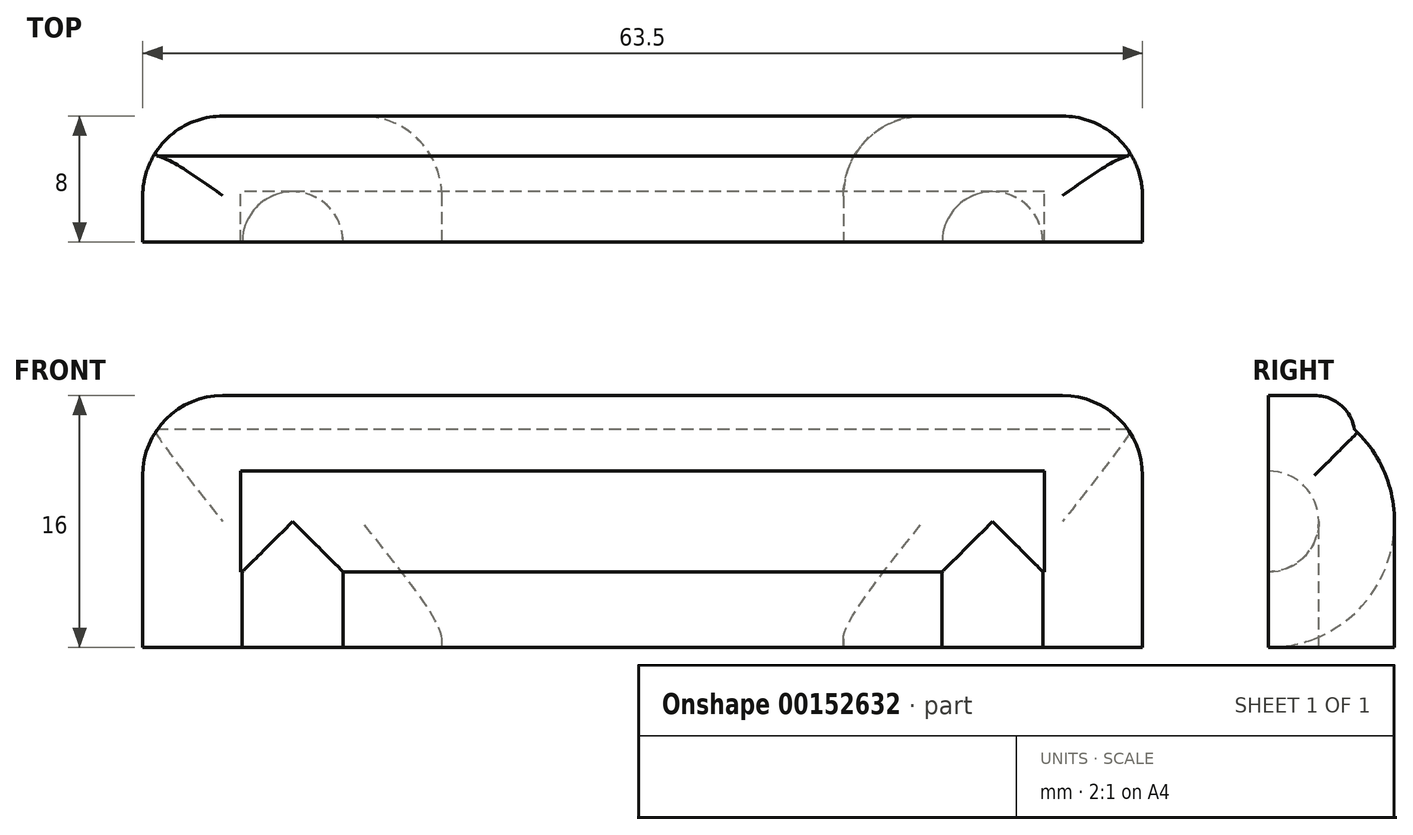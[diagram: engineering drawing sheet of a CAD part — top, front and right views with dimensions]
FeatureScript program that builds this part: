
annotation { "Feature Type Name" : "Feature", "Feature Type Description" : "" }
export const myFeature = defineFeature(function(context is Context, id is Id, definition is map)
    precondition{}
    {
        {
            var Q0;
            Q0=qCreatedBy(makeId("Right.planeOp"),FACE);
            var sketch = newSketch(context, id + "F0", { "sketchPlane" : qUnion([Q0])});
            skCircle(sketch, "E0", {"center": v(0, 0) * mm, "radius": 8 * mm});
            skSolve(sketch);
        }
        {
            var Q0;
            Q0 = qSketchRegion(id + "F0", true);
            extrude(context, id + "F1", {"entities" : qUnion([Q0]), "depth" : 63.5 * mm});
        }
        {
            var Q0;
            Q0=qCreatedBy(makeId("Top.planeOp"),FACE);
            var sketch = newSketch(context, id + "F2", { "sketchPlane" : qUnion([Q0])});
            skLineSegment(sketch, "E1.bottom", {"start": v(0, -8) * mm, "end": v(19, -8) * mm});
            skLineSegment(sketch, "E1.top", {"start": v(0, 8) * mm, "end": v(19, 8) * mm});
            skLineSegment(sketch, "E1.left", {"start": v(0, -8) * mm, "end": v(0, 8) * mm});
            skLineSegment(sketch, "E1.right", {"start": v(19, -8) * mm, "end": v(19, 8) * mm});
            skLineSegment(sketch, "E2.bottom", {"start": v(63.5, 8) * mm, "end": v(44.5, 8) * mm});
            skLineSegment(sketch, "E2.top", {"start": v(63.5, -8) * mm, "end": v(44.5, -8) * mm});
            skLineSegment(sketch, "E2.left", {"start": v(63.5, 8) * mm, "end": v(63.5, -8) * mm});
            skLineSegment(sketch, "E2.right", {"start": v(44.5, 8) * mm, "end": v(44.5, -8) * mm});
            skSolve(sketch);
        }
        {
            var Q0;
            Q0 = qSketchRegion(id + "F2", true);
            extrude(context, id + "F3", {"entities" : qUnion([Q0]), "operationType" : NewBodyOperationType.ADD, "oppositeDirection" : true, "depth" : 16 * mm / 2});
        }
        {
            var Q0;
            Q0=qCreatedBy(makeId("Top.planeOp"),FACE);
            var sketch = newSketch(context, id + "F4", { "sketchPlane" : qUnion([Q0])});
            skCircle(sketch, "E3", {"center": v(9.53, 0) * mm, "radius": 3.2 * mm});
            skCircle(sketch, "E4", {"center": v(53.98, 0) * mm, "radius": 3.2 * mm});
            skSolve(sketch);
        }
        {
            var Q0;
            Q0 = qSketchRegion(id + "F4", true);
            extrude(context, id + "F5", {"entities" : qUnion([Q0]), "operationType" : NewBodyOperationType.REMOVE, "oppositeDirection" : true, "depth" : 25.4 * mm});
        }
        {
            var Q0;
            Q0=qCreatedBy(makeId("Right.planeOp"),FACE);
            cPlane(context, id + "F6", {"entities" : qUnion([Q0]), "cplaneType" : CPlaneType.OFFSET, "offset" : 9.52 * mm, "width" : 152.4 * mm, "height" : 152.4 * mm});
        }
        {
            var Q0;
            Q0=qCreatedBy(id+"F6.planeOp",FACE);
            var sketch = newSketch(context, id + "F7", { "sketchPlane" : qUnion([Q0])});
            skCircle(sketch, "E5", {"center": v(0, 0) * mm, "radius": 3.2 * mm});
            skSolve(sketch);
        }
        {
            var Q0;
            Q0 = qSketchRegion(id + "F7", true);
            extrude(context, id + "F8", {"entities" : qUnion([Q0]), "operationType" : NewBodyOperationType.REMOVE, "depth" : 47.75 * mm, "hasSecondDirection" : true, "secondDirectionOppositeDirection" : true, "secondDirectionDepth" : 3.3 * mm});
        }
        {
            var Q0;
            Q0=makeQuery(id+"F3.boolean.opBoolean","MERGE",FACE,{"derivedFrom":[makeQuery(id+"F1.opExtrude","CAP_FACE",FACE,{"disambiguationData":[OSD([sQuery(id+"F0.wireOp",EDGE,"E0")])],"isStart":false}),makeQuery(id+"F3.opExtrude","SWEPT_FACE",FACE,{"disambiguationData":[OSD([sQuery(id+"F2.wireOp",EDGE,"E2.left")])]})]});
            var sketch = newSketch(context, id + "F9", { "sketchPlane" : qUnion([Q0])});
            skLineSegment(sketch, "E6.bottom", {"start": v(-5.46, 8) * mm, "end": v(5.46, 8) * mm});
            skLineSegment(sketch, "E6.top", {"start": v(-5.46, 5.46) * mm, "end": v(5.46, 5.46) * mm});
            skLineSegment(sketch, "E6.left", {"start": v(-5.46, 8) * mm, "end": v(-5.46, 5.46) * mm});
            skLineSegment(sketch, "E6.right", {"start": v(5.46, 8) * mm, "end": v(5.46, 5.46) * mm});
            skSolve(sketch);
        }
        {
            var Q0;
            Q0 = qSketchRegion(id + "F9", true);
            extrude(context, id + "F10", {"entities" : qUnion([Q0]), "operationType" : NewBodyOperationType.ADD, "oppositeDirection" : true, "depth" : 63.5 * mm});
        }
        {
            var Q0;
            Q0=makeQuery(id+"F3.opExtrude","SWEPT_EDGE",EDGE,{"disambiguationData":[OSD([sQuery(id+"F2.wireOp",EDGE,"E1.bottom"),sQuery(id+"F2.wireOp",EDGE,"E1.left")])]});
            var Q1;
            Q1=makeQuery(id+"F3.opExtrude","SWEPT_EDGE",EDGE,{"disambiguationData":[OSD([sQuery(id+"F2.wireOp",EDGE,"E1.top"),sQuery(id+"F2.wireOp",EDGE,"E1.left")])]});
            var Q2;
            Q2=makeQuery(id+"F3.opExtrude","SWEPT_EDGE",EDGE,{"disambiguationData":[OSD([sQuery(id+"F2.wireOp",EDGE,"E2.bottom"),sQuery(id+"F2.wireOp",EDGE,"E2.left")])]});
            var Q3;
            Q3=makeQuery(id+"F3.opExtrude","SWEPT_EDGE",EDGE,{"disambiguationData":[OSD([sQuery(id+"F2.wireOp",EDGE,"E2.top"),sQuery(id+"F2.wireOp",EDGE,"E2.left")])]});
            var Q4;
            Q4=makeQuery(id+"F3.opExtrude","SWEPT_EDGE",EDGE,{"disambiguationData":[OSD([sQuery(id+"F2.wireOp",EDGE,"E1.top"),sQuery(id+"F2.wireOp",EDGE,"E1.right")])]});
            var Q5;
            Q5=makeQuery(id+"F3.opExtrude","SWEPT_EDGE",EDGE,{"disambiguationData":[OSD([sQuery(id+"F2.wireOp",EDGE,"E2.bottom"),sQuery(id+"F2.wireOp",EDGE,"E2.right")])]});
            var Q6;
            Q6=makeQuery(id+"F3.opExtrude","SWEPT_EDGE",EDGE,{"disambiguationData":[OSD([sQuery(id+"F2.wireOp",EDGE,"E2.top"),sQuery(id+"F2.wireOp",EDGE,"E2.right")])]});
            var Q7;
            Q7=makeQuery(id+"F3.opExtrude","SWEPT_EDGE",EDGE,{"disambiguationData":[OSD([sQuery(id+"F2.wireOp",EDGE,"E1.bottom"),sQuery(id+"F2.wireOp",EDGE,"E1.right")])]});
            fillet(context, id + "F11", {"entities" : qUnion([Q0, Q1, Q2, Q3, Q4, Q5, Q6, Q7]), "radius" : 5.08 * mm, "tangentPropagation" : true, "allowEdgeOverflow" : false});
        }
        {
            var Q0;
            Q0=makeQuery(id+"F10.opExtrude","SWEPT_EDGE",EDGE,{"disambiguationData":[OSD([sQuery(id+"F9.wireOp",EDGE,"E6.bottom"),sQuery(id+"F9.wireOp",EDGE,"E6.right")])]});
            var Q1;
            Q1=makeQuery(id+"F10.opExtrude","SWEPT_EDGE",EDGE,{"disambiguationData":[OSD([sQuery(id+"F9.wireOp",EDGE,"E6.bottom"),sQuery(id+"F9.wireOp",EDGE,"E6.left")])]});
            fillet(context, id + "F12", {"entities" : qUnion([Q0, Q1]), "radius" : 2.54 * mm, "tangentPropagation" : true, "allowEdgeOverflow" : false});
        }
        {
            var Q0;
            Q0=makeQuery(id+"F10.opExtrude","CAP_EDGE",EDGE,{"disambiguationData":[OSD([sQuery(id+"F9.wireOp",EDGE,"E6.bottom")])],"isStart":true});
            var Q1;
            Q1=makeQuery(id+"F10.opExtrude","CAP_EDGE",EDGE,{"disambiguationData":[OSD([sQuery(id+"F9.wireOp",EDGE,"E6.bottom")])],"isStart":false});
            fillet(context, id + "F13", {"entities" : qUnion([Q0, Q1]), "radius" : 5.08 * mm, "tangentPropagation" : true, "allowEdgeOverflow" : false});
        }
        {
            var Q0;
            Q0=qCreatedBy(makeId("Front.planeOp"),FACE);
            var sketch = newSketch(context, id + "F14", { "sketchPlane" : qUnion([Q0])});
            skLineSegment(sketch, "E7.bottom", {"start": v(-2.31, -11.6) * mm, "end": v(65.9, -11.6) * mm});
            skLineSegment(sketch, "E7.top", {"start": v(-2.31, 11.33) * mm, "end": v(65.9, 11.33) * mm});
            skLineSegment(sketch, "E7.left", {"start": v(-2.31, -11.6) * mm, "end": v(-2.31, 11.33) * mm});
            skLineSegment(sketch, "E7.right", {"start": v(65.9, -11.6) * mm, "end": v(65.9, 11.33) * mm});
            skSolve(sketch);
        }
        {
            var Q0;
            Q0 = qSketchRegion(id + "F14", true);
            extrude(context, id + "F15", {"entities" : qUnion([Q0]), "operationType" : NewBodyOperationType.REMOVE, "depth" : 25.4 * mm});
        }
    });
